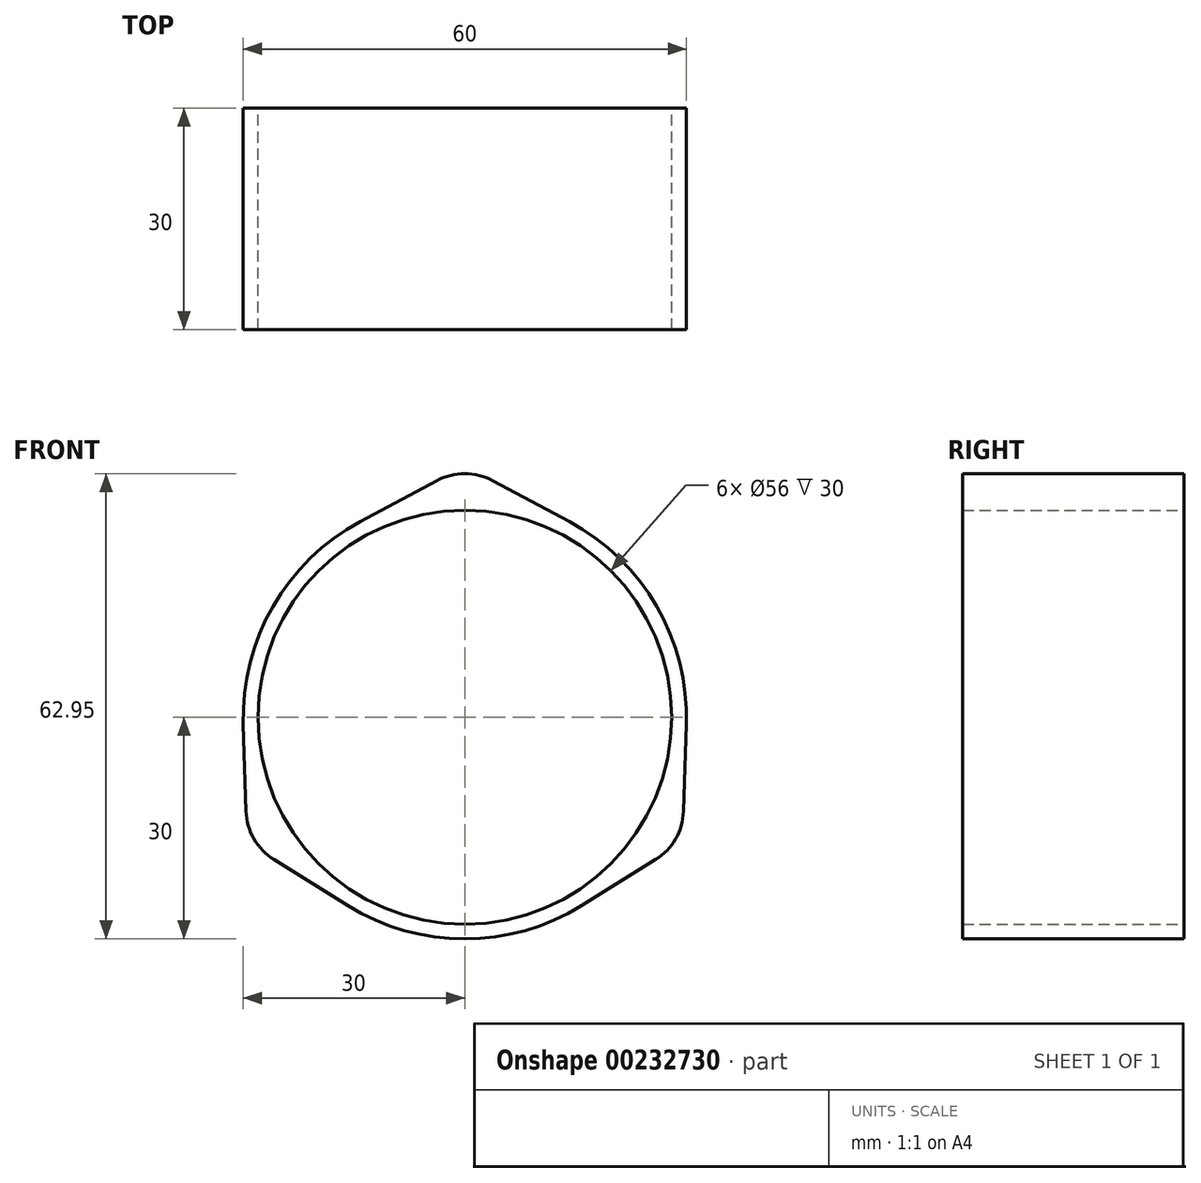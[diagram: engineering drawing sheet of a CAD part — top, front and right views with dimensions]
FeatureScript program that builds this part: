
annotation { "Feature Type Name" : "Feature", "Feature Type Description" : "" }
export const myFeature = defineFeature(function(context is Context, id is Id, definition is map)
    precondition{}
    {
        {
            var Q0;
            Q0=qCreatedBy(makeId("Front.planeOp"),FACE);
            var sketch = newSketch(context, id + "F0", { "sketchPlane" : qUnion([Q0])});
            skCircle(sketch, "E0", {"center": v(0, 0) * mm, "radius": 28 * mm});
            skArc(sketch, "E1", {"start": v(-14.15, 26.45) * mm, "mid": v(-25.98, 15) * mm, "end": v(-29.98, -0.97) * mm});
            skLineSegment(sketch, "E2", {"start": v(-14.15, 26.45) * mm, "end": v(-3.77, 32) * mm});
            skLineSegment(sketch, "E3", {"start": v(3.77, 32) * mm, "end": v(14.15, 26.45) * mm});
            skPoint(sketch, "E4.visualSharp", {"position": v(0, 34.02) * mm});
            skArc(sketch, "E4.filletArc", {"start": v(3.77, 32) * mm, "mid": v(0, 32.95) * mm, "end": v(-3.77, 32) * mm});
            skLineSegment(sketch, "E5.1.0", {"start": v(29.98, -0.97) * mm, "end": v(29.6, -12.73) * mm});
            skArc(sketch, "E5.1.1", {"start": v(25.83, -19.27) * mm, "mid": v(28.54, -16.47) * mm, "end": v(29.6, -12.73) * mm});
            skLineSegment(sketch, "E5.1.2", {"start": v(25.83, -19.27) * mm, "end": v(15.83, -25.48) * mm});
            skLineSegment(sketch, "E5.2.0", {"start": v(-15.83, -25.48) * mm, "end": v(-25.83, -19.27) * mm});
            skArc(sketch, "E5.2.1", {"start": v(-29.6, -12.73) * mm, "mid": v(-28.54, -16.47) * mm, "end": v(-25.83, -19.27) * mm});
            skLineSegment(sketch, "E5.2.2", {"start": v(-29.6, -12.73) * mm, "end": v(-29.98, -0.97) * mm});
            skLineSegment(sketch, "E5.anchor1", {"start": v(0, 0) * mm, "end": v(-14.15, 26.45) * mm, "construction": true});
            skLineSegment(sketch, "E5.anchor2", {"start": v(0, 0) * mm, "end": v(-15.83, -25.48) * mm, "construction": true});
            skArc(sketch, "E6.trimOffspring", {"start": v(-15.83, -25.48) * mm, "mid": v(0, -30) * mm, "end": v(15.83, -25.48) * mm});
            skArc(sketch, "E7.trimOffspring", {"start": v(29.98, -0.97) * mm, "mid": v(25.98, 15) * mm, "end": v(14.15, 26.45) * mm});
            skSolve(sketch);
        }
        {
            var Q0;
            Q0=makeQuery(id+"F0.imprint","IMPRINT",FACE,{"disambiguationData":[TD([[makeQuery(id+"F0.imprint","IMPRINT",EDGE,{"derivedFrom":sQuery(id+"F0.wireOp",EDGE,"E0")}),-1.0]])]});
            extrude(context, id + "F1", {"entities" : qUnion([Q0]), "depth" : 30 * mm});
        }
    });
